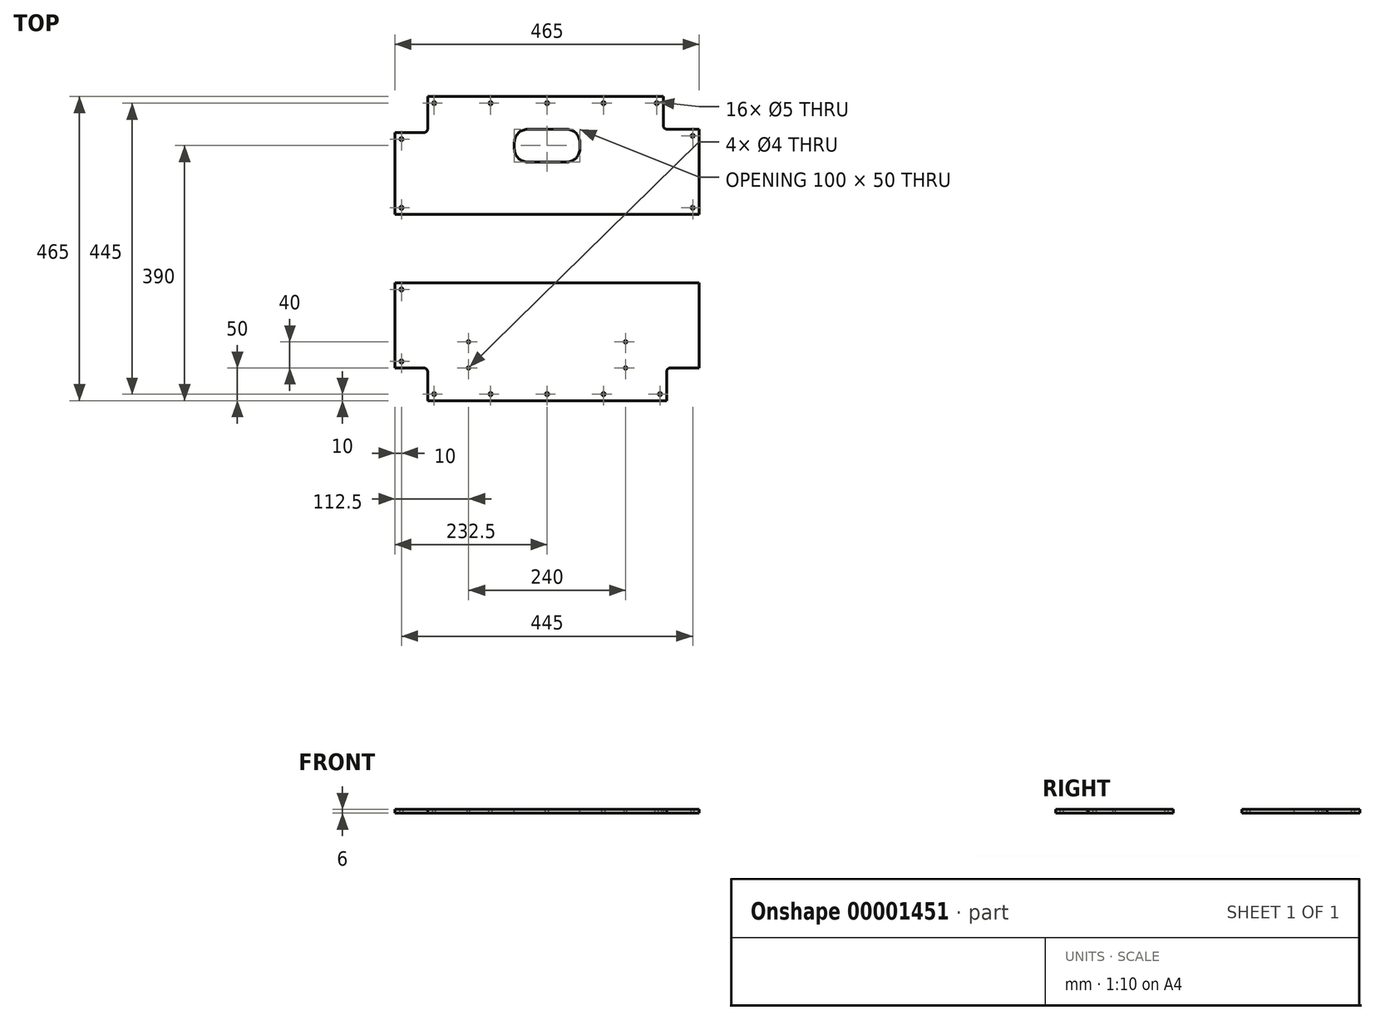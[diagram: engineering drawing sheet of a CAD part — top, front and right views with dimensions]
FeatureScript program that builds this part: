
annotation { "Feature Type Name" : "Feature", "Feature Type Description" : "" }
export const myFeature = defineFeature(function(context is Context, id is Id, definition is map)
    precondition{}
    {
        {
            var Q0;
            Q0=qCreatedBy(makeId("Top.planeOp"),FACE);
            var sketch = newSketch(context, id + "F0", { "sketchPlane" : qUnion([Q0])});
            skLineSegment(sketch, "E0.rect.bottom", {"start": v(212.5, 212.5) * mm, "end": v(-212.5, 212.5) * mm, "construction": true});
            skLineSegment(sketch, "E0.rect.top", {"start": v(212.5, -212.5) * mm, "end": v(-212.5, -212.5) * mm, "construction": true});
            skLineSegment(sketch, "E0.rect.left", {"start": v(212.5, 212.5) * mm, "end": v(212.5, -212.5) * mm, "construction": true});
            skLineSegment(sketch, "E0.rect.right", {"start": v(-212.5, 212.5) * mm, "end": v(-212.5, -212.5) * mm, "construction": true});
            skPoint(sketch, "E0.rect.middle", {"position": v(0, 0) * mm});
            skLineSegment(sketch, "E1.rect.bottom", {"start": v(232.5, 232.5) * mm, "end": v(-232.5, 232.5) * mm, "construction": true});
            skLineSegment(sketch, "E1.rect.top", {"start": v(232.5, -232.5) * mm, "end": v(-232.5, -232.5) * mm, "construction": true});
            skLineSegment(sketch, "E1.rect.left", {"start": v(232.5, 232.5) * mm, "end": v(232.5, -232.5) * mm, "construction": true});
            skLineSegment(sketch, "E1.rect.right", {"start": v(-232.5, 232.5) * mm, "end": v(-232.5, -232.5) * mm, "construction": true});
            skLineSegment(sketch, "E2", {"start": v(-212.5, 212.5) * mm, "end": v(-232.5, 212.5) * mm, "construction": true});
            skLineSegment(sketch, "E3", {"start": v(-212.5, 232.5) * mm, "end": v(-212.5, 212.5) * mm, "construction": true});
            skLineSegment(sketch, "E4", {"start": v(-212.5, -212.5) * mm, "end": v(-232.5, -212.5) * mm, "construction": true});
            skLineSegment(sketch, "E5", {"start": v(-212.5, -232.5) * mm, "end": v(-212.5, -212.5) * mm, "construction": true});
            skLineSegment(sketch, "E6", {"start": v(212.5, -212.5) * mm, "end": v(212.5, -232.5) * mm, "construction": true});
            skLineSegment(sketch, "E7", {"start": v(232.5, -212.5) * mm, "end": v(212.5, -212.5) * mm, "construction": true});
            skLineSegment(sketch, "E8", {"start": v(212.5, 212.5) * mm, "end": v(212.5, 232.5) * mm, "construction": true});
            skLineSegment(sketch, "E9", {"start": v(232.5, 212.5) * mm, "end": v(212.5, 212.5) * mm, "construction": true});
            skLineSegment(sketch, "E10", {"start": v(177.5, 232.5) * mm, "end": v(177.5, 182.5) * mm});
            skLineSegment(sketch, "E11", {"start": v(177.5, 182.5) * mm, "end": v(232.5, 182.5) * mm});
            skLineSegment(sketch, "E12", {"start": v(232.5, 182.5) * mm, "end": v(232.5, 52.5) * mm});
            skLineSegment(sketch, "E13", {"start": v(232.5, 52.5) * mm, "end": v(-232.5, 52.5) * mm});
            skLineSegment(sketch, "E14", {"start": v(-232.5, 52.5) * mm, "end": v(-232.5, 177.5) * mm});
            skLineSegment(sketch, "E15", {"start": v(-232.5, 177.5) * mm, "end": v(-182.5, 177.5) * mm});
            skLineSegment(sketch, "E16", {"start": v(-182.5, 177.5) * mm, "end": v(-182.5, 232.5) * mm});
            skLineSegment(sketch, "E17", {"start": v(-182.5, 232.5) * mm, "end": v(177.5, 232.5) * mm});
            skLineSegment(sketch, "E18", {"start": v(-232.5, -52.5) * mm, "end": v(232.5, -52.5) * mm});
            skLineSegment(sketch, "E19", {"start": v(232.5, -52.5) * mm, "end": v(232.5, -182.5) * mm});
            skLineSegment(sketch, "E20", {"start": v(232.5, -182.5) * mm, "end": v(182.5, -182.5) * mm});
            skLineSegment(sketch, "E21", {"start": v(182.5, -182.5) * mm, "end": v(182.5, -232.5) * mm});
            skLineSegment(sketch, "E22", {"start": v(182.5, -232.5) * mm, "end": v(-182.5, -232.5) * mm});
            skLineSegment(sketch, "E23", {"start": v(-182.5, -232.5) * mm, "end": v(-182.5, -182.5) * mm});
            skLineSegment(sketch, "E24", {"start": v(-182.5, -182.5) * mm, "end": v(-232.5, -182.5) * mm});
            skLineSegment(sketch, "E25", {"start": v(-232.5, -182.5) * mm, "end": v(-232.5, -52.5) * mm});
            skLineSegment(sketch, "E26", {"start": v(-182.5, -182.5) * mm, "end": v(182.5, -182.5) * mm, "construction": true});
            skSolve(sketch);
        }
        {
            var Q0;
            {Q0=qUnion([makeQuery(id+"F0.imprint","IMPRINT",FACE,{"disambiguationData":[TD([[makeQuery(id+"F0.imprint","IMPRINT",EDGE,{"derivedFrom":sQuery(id+"F0.wireOp",EDGE,"E10")}),-1.0]])]}),makeQuery(id+"F0.imprint","IMPRINT",FACE,{"disambiguationData":[TD([[makeQuery(id+"F0.imprint","IMPRINT",EDGE,{"derivedFrom":sQuery(id+"F0.wireOp",EDGE,"E18")}),-1.0]])]})]);}
            extrude(context, id + "F1", {"entities" : qUnion([Q0]), "depth" : 6 * mm});
        }
        {
            var Q0;
            Q0=makeQuery(id+"F1.opExtrude","SWEPT_EDGE",EDGE,{"disambiguationData":[OSD([sQuery(id+"F0.wireOp",EDGE,"E23"),sQuery(id+"F0.wireOp",EDGE,"E24")])]});
            var Q1;
            Q1=makeQuery(id+"F1.opExtrude","SWEPT_EDGE",EDGE,{"disambiguationData":[OSD([sQuery(id+"F0.wireOp",EDGE,"E20"),sQuery(id+"F0.wireOp",EDGE,"E21")])]});
            var Q2;
            Q2=makeQuery(id+"F1.opExtrude","SWEPT_EDGE",EDGE,{"disambiguationData":[OSD([sQuery(id+"F0.wireOp",EDGE,"E10"),sQuery(id+"F0.wireOp",EDGE,"E11")])]});
            var Q3;
            Q3=makeQuery(id+"F1.opExtrude","SWEPT_EDGE",EDGE,{"disambiguationData":[OSD([sQuery(id+"F0.wireOp",EDGE,"E15"),sQuery(id+"F0.wireOp",EDGE,"E16")])]});
            fillet(context, id + "F2", {"entities" : qUnion([Q0, Q1, Q2, Q3]), "radius" : 6 * mm, "tangentPropagation" : true, "allowEdgeOverflow" : false});
        }
        {
            var Q0;
            Q0=makeQuery(id+"F1.opExtrude","CAP_FACE",FACE,{"disambiguationData":[OSD([sQuery(id+"F0.wireOp",EDGE,"E18"),sQuery(id+"F0.wireOp",EDGE,"E19"),sQuery(id+"F0.wireOp",EDGE,"E20"),sQuery(id+"F0.wireOp",EDGE,"E21"),sQuery(id+"F0.wireOp",EDGE,"E22"),sQuery(id+"F0.wireOp",EDGE,"E23"),sQuery(id+"F0.wireOp",EDGE,"E24"),sQuery(id+"F0.wireOp",EDGE,"E25")])],"isStart":false});
            var sketch = newSketch(context, id + "F3", { "sketchPlane" : qUnion([Q0])});
            skLineSegment(sketch, "E27", {"start": v(-182.5, -222.5) * mm, "end": v(-172.5, -222.5) * mm, "construction": true});
            skLineSegment(sketch, "E28", {"start": v(-172.5, -222.5) * mm, "end": v(-86.25, -222.5) * mm, "construction": true});
            skLineSegment(sketch, "E29", {"start": v(-86.25, -222.5) * mm, "end": v(0, -222.5) * mm, "construction": true});
            skLineSegment(sketch, "E30", {"start": v(0, -222.5) * mm, "end": v(86.25, -222.5) * mm, "construction": true});
            skLineSegment(sketch, "E31", {"start": v(86.25, -222.5) * mm, "end": v(172.5, -222.5) * mm, "construction": true});
            skLineSegment(sketch, "E32", {"start": v(172.5, -222.5) * mm, "end": v(182.5, -222.5) * mm, "construction": true});
            skLineSegment(sketch, "E33", {"start": v(0, -222.5) * mm, "end": v(0, -232.5) * mm, "construction": true});
            skCircle(sketch, "E34", {"center": v(-172.5, -222.5) * mm, "radius": 2.5 * mm});
            skCircle(sketch, "E35", {"center": v(-86.25, -222.5) * mm, "radius": 2.5 * mm});
            skCircle(sketch, "E36", {"center": v(0, -222.5) * mm, "radius": 2.5 * mm});
            skCircle(sketch, "E37", {"center": v(86.25, -222.5) * mm, "radius": 2.5 * mm});
            skCircle(sketch, "E38", {"center": v(172.5, -222.5) * mm, "radius": 2.5 * mm});
            skLineSegment(sketch, "E39", {"start": v(-222.5, -52.5) * mm, "end": v(-222.5, -62.5) * mm, "construction": true});
            skLineSegment(sketch, "E40", {"start": v(-222.5, -62.5) * mm, "end": v(-222.5, -172.5) * mm, "construction": true});
            skLineSegment(sketch, "E41", {"start": v(-222.5, -172.5) * mm, "end": v(-222.5, -182.5) * mm, "construction": true});
            skLineSegment(sketch, "E42", {"start": v(-222.5, -62.5) * mm, "end": v(-232.5, -62.5) * mm, "construction": true});
            skLineSegment(sketch, "E43", {"start": v(-222.5, -172.5) * mm, "end": v(-232.5, -172.5) * mm, "construction": true});
            skLineSegment(sketch, "E44", {"start": v(0, -222.5) * mm, "end": v(0, -52.5) * mm, "construction": true});
            skCircle(sketch, "E45", {"center": v(-222.5, -62.5) * mm, "radius": 2.5 * mm});
            skCircle(sketch, "E46", {"center": v(-222.5, -172.5) * mm, "radius": 2.5 * mm});
            skCircle(sketch, "E47.0.MirrorC", {"center": v(222.5, -62.5) * mm, "radius": 2.5 * mm});
            skCircle(sketch, "E47.1.MirrorC", {"center": v(222.5, -172.5) * mm, "radius": 2.5 * mm});
            skSolve(sketch);
        }
        {
            var Q0;
            {Q0=qUnion([makeQuery(id+"F3.imprint","IMPRINT",FACE,{"disambiguationData":[TD([[makeQuery(id+"F3.imprint","IMPRINT",EDGE,{"derivedFrom":sQuery(id+"F3.wireOp",EDGE,"E34")}),1.0]])]}),makeQuery(id+"F3.imprint","IMPRINT",FACE,{"disambiguationData":[TD([[makeQuery(id+"F3.imprint","IMPRINT",EDGE,{"derivedFrom":sQuery(id+"F3.wireOp",EDGE,"E35")}),1.0]])]}),makeQuery(id+"F3.imprint","IMPRINT",FACE,{"disambiguationData":[TD([[makeQuery(id+"F3.imprint","IMPRINT",EDGE,{"derivedFrom":sQuery(id+"F3.wireOp",EDGE,"E36")}),1.0]])]}),makeQuery(id+"F3.imprint","IMPRINT",FACE,{"disambiguationData":[TD([[makeQuery(id+"F3.imprint","IMPRINT",EDGE,{"derivedFrom":sQuery(id+"F3.wireOp",EDGE,"E37")}),1.0]])]}),makeQuery(id+"F3.imprint","IMPRINT",FACE,{"disambiguationData":[TD([[makeQuery(id+"F3.imprint","IMPRINT",EDGE,{"derivedFrom":sQuery(id+"F3.wireOp",EDGE,"E38")}),1.0]])]}),makeQuery(id+"F3.imprint","IMPRINT",FACE,{"disambiguationData":[TD([[makeQuery(id+"F3.imprint","IMPRINT",EDGE,{"derivedFrom":sQuery(id+"F3.wireOp",EDGE,"E45")}),1.0]])]}),makeQuery(id+"F3.imprint","IMPRINT",FACE,{"disambiguationData":[TD([[makeQuery(id+"F3.imprint","IMPRINT",EDGE,{"derivedFrom":sQuery(id+"F3.wireOp",EDGE,"E46")}),1.0]])]}),makeQuery(id+"F3.imprint","IMPRINT",FACE,{"disambiguationData":[TD([[makeQuery(id+"F3.imprint","IMPRINT",EDGE,{"derivedFrom":sQuery(id+"F3.wireOp",EDGE,"E47.0.MirrorC")}),-1.0]])]}),makeQuery(id+"F3.imprint","IMPRINT",FACE,{"disambiguationData":[TD([[makeQuery(id+"F3.imprint","IMPRINT",EDGE,{"derivedFrom":sQuery(id+"F3.wireOp",EDGE,"E47.1.MirrorC")}),-1.0]])]})]);}
            extrude(context, id + "F4", {"entities" : qUnion([Q0]), "operationType" : NewBodyOperationType.REMOVE, "endBound" : BoundingType.THROUGH_ALL, "oppositeDirection" : true, "depth" : 25 * mm});
        }
        {
            var Q0;
            Q0=makeQuery(id+"F1.opExtrude","CAP_FACE",FACE,{"disambiguationData":[OSD([sQuery(id+"F0.wireOp",EDGE,"E18"),sQuery(id+"F0.wireOp",EDGE,"E19"),sQuery(id+"F0.wireOp",EDGE,"E20"),sQuery(id+"F0.wireOp",EDGE,"E21"),sQuery(id+"F0.wireOp",EDGE,"E22"),sQuery(id+"F0.wireOp",EDGE,"E23"),sQuery(id+"F0.wireOp",EDGE,"E24"),sQuery(id+"F0.wireOp",EDGE,"E25")])],"isStart":false});
            var sketch = newSketch(context, id + "F5", { "sketchPlane" : qUnion([Q0])});
            skLineSegment(sketch, "E48", {"start": v(0, -232.5) * mm, "end": v(0, -162.5) * mm, "construction": true});
            skLineSegment(sketch, "E49.rect.bottom", {"start": v(120, -142.5) * mm, "end": v(-120, -142.5) * mm, "construction": true});
            skLineSegment(sketch, "E49.rect.top", {"start": v(120, -182.5) * mm, "end": v(-120, -182.5) * mm, "construction": true});
            skLineSegment(sketch, "E49.rect.left", {"start": v(120, -142.5) * mm, "end": v(120, -182.5) * mm, "construction": true});
            skLineSegment(sketch, "E49.rect.right", {"start": v(-120, -142.5) * mm, "end": v(-120, -182.5) * mm, "construction": true});
            skPoint(sketch, "E49.rect.middle", {"position": v(0, -162.5) * mm});
            skCircle(sketch, "E50", {"center": v(-120, -142.5) * mm, "radius": 2 * mm});
            skCircle(sketch, "E51", {"center": v(120, -142.5) * mm, "radius": 2 * mm});
            skCircle(sketch, "E52", {"center": v(-120, -182.5) * mm, "radius": 2 * mm});
            skCircle(sketch, "E53", {"center": v(120, -182.5) * mm, "radius": 2 * mm});
            skSolve(sketch);
        }
        {
            var Q0;
            {Q0=qUnion([makeQuery(id+"F5.imprint","IMPRINT",FACE,{"disambiguationData":[TD([[makeQuery(id+"F5.imprint","IMPRINT",EDGE,{"derivedFrom":sQuery(id+"F5.wireOp",EDGE,"E50")}),1.0]])]}),makeQuery(id+"F5.imprint","IMPRINT",FACE,{"disambiguationData":[TD([[makeQuery(id+"F5.imprint","IMPRINT",EDGE,{"derivedFrom":sQuery(id+"F5.wireOp",EDGE,"E51")}),1.0]])]}),makeQuery(id+"F5.imprint","IMPRINT",FACE,{"disambiguationData":[TD([[makeQuery(id+"F5.imprint","IMPRINT",EDGE,{"derivedFrom":sQuery(id+"F5.wireOp",EDGE,"E52")}),1.0]])]}),makeQuery(id+"F5.imprint","IMPRINT",FACE,{"disambiguationData":[TD([[makeQuery(id+"F5.imprint","IMPRINT",EDGE,{"derivedFrom":sQuery(id+"F5.wireOp",EDGE,"E53")}),1.0]])]})]);}
            extrude(context, id + "F6", {"entities" : qUnion([Q0]), "operationType" : NewBodyOperationType.REMOVE, "endBound" : BoundingType.THROUGH_ALL, "oppositeDirection" : true, "depth" : 25 * mm});
        }
        {
            var Q0;
            Q0=makeQuery(id+"F1.opExtrude","CAP_FACE",FACE,{"disambiguationData":[OSD([sQuery(id+"F0.wireOp",EDGE,"E10"),sQuery(id+"F0.wireOp",EDGE,"E11"),sQuery(id+"F0.wireOp",EDGE,"E12"),sQuery(id+"F0.wireOp",EDGE,"E13"),sQuery(id+"F0.wireOp",EDGE,"E14"),sQuery(id+"F0.wireOp",EDGE,"E15"),sQuery(id+"F0.wireOp",EDGE,"E16"),sQuery(id+"F0.wireOp",EDGE,"E17")])],"isStart":false});
            var sketch = newSketch(context, id + "F7", { "sketchPlane" : qUnion([Q0])});
            skLineSegment(sketch, "E54", {"start": v(-182.5, 222.5) * mm, "end": v(-172.5, 222.5) * mm, "construction": true});
            skLineSegment(sketch, "E55", {"start": v(-172.5, 222.5) * mm, "end": v(-86.25, 222.5) * mm, "construction": true});
            skLineSegment(sketch, "E56", {"start": v(-86.25, 222.5) * mm, "end": v(0, 222.5) * mm, "construction": true});
            skLineSegment(sketch, "E57", {"start": v(0, 222.5) * mm, "end": v(0, 232.5) * mm, "construction": true});
            skLineSegment(sketch, "E58", {"start": v(0, 222.5) * mm, "end": v(0, 52.5) * mm, "construction": true});
            skLineSegment(sketch, "E59", {"start": v(0, 222.5) * mm, "end": v(86.25, 222.5) * mm, "construction": true});
            skLineSegment(sketch, "E60", {"start": v(86.25, 222.5) * mm, "end": v(167.5, 222.5) * mm, "construction": true});
            skLineSegment(sketch, "E61", {"start": v(167.5, 222.5) * mm, "end": v(177.5, 222.5) * mm, "construction": true});
            skLineSegment(sketch, "E62", {"start": v(-222.5, 177.5) * mm, "end": v(-222.5, 167.5) * mm, "construction": true});
            skLineSegment(sketch, "E63", {"start": v(-222.5, 167.5) * mm, "end": v(-222.5, 62.5) * mm, "construction": true});
            skLineSegment(sketch, "E64", {"start": v(-222.5, 62.5) * mm, "end": v(-222.5, 52.5) * mm, "construction": true});
            skLineSegment(sketch, "E65", {"start": v(-222.5, 167.5) * mm, "end": v(-232.5, 167.5) * mm, "construction": true});
            skLineSegment(sketch, "E66", {"start": v(222.5, 182.5) * mm, "end": v(222.5, 172.5) * mm, "construction": true});
            skLineSegment(sketch, "E67", {"start": v(222.5, 172.5) * mm, "end": v(232.5, 172.5) * mm, "construction": true});
            skLineSegment(sketch, "E68", {"start": v(222.5, 172.5) * mm, "end": v(222.5, 62.5) * mm, "construction": true});
            skLineSegment(sketch, "E69", {"start": v(222.5, 62.5) * mm, "end": v(232.5, 62.5) * mm, "construction": true});
            skCircle(sketch, "E70", {"center": v(-222.5, 167.5) * mm, "radius": 2.5 * mm});
            skCircle(sketch, "E71", {"center": v(-222.5, 62.5) * mm, "radius": 2.5 * mm});
            skCircle(sketch, "E72", {"center": v(-172.5, 222.5) * mm, "radius": 2.5 * mm});
            skCircle(sketch, "E73", {"center": v(-86.25, 222.5) * mm, "radius": 2.5 * mm});
            skCircle(sketch, "E74", {"center": v(0, 222.5) * mm, "radius": 2.5 * mm});
            skCircle(sketch, "E75", {"center": v(86.25, 222.5) * mm, "radius": 2.5 * mm});
            skCircle(sketch, "E76", {"center": v(167.5, 222.5) * mm, "radius": 2.5 * mm});
            skCircle(sketch, "E77", {"center": v(222.5, 172.5) * mm, "radius": 2.5 * mm});
            skCircle(sketch, "E78", {"center": v(222.5, 62.5) * mm, "radius": 2.5 * mm});
            skLineSegment(sketch, "E79", {"start": v(222.5, 62.5) * mm, "end": v(222.5, 52.5) * mm, "construction": true});
            skLineSegment(sketch, "E80", {"start": v(-222.5, 62.5) * mm, "end": v(-232.5, 62.5) * mm, "construction": true});
            skSolve(sketch);
        }
        {
            var Q0;
            {Q0=qUnion([makeQuery(id+"F7.imprint","IMPRINT",FACE,{"disambiguationData":[TD([[makeQuery(id+"F7.imprint","IMPRINT",EDGE,{"derivedFrom":sQuery(id+"F7.wireOp",EDGE,"E70")}),1.0]])]}),makeQuery(id+"F7.imprint","IMPRINT",FACE,{"disambiguationData":[TD([[makeQuery(id+"F7.imprint","IMPRINT",EDGE,{"derivedFrom":sQuery(id+"F7.wireOp",EDGE,"E71")}),1.0]])]}),makeQuery(id+"F7.imprint","IMPRINT",FACE,{"disambiguationData":[TD([[makeQuery(id+"F7.imprint","IMPRINT",EDGE,{"derivedFrom":sQuery(id+"F7.wireOp",EDGE,"E72")}),1.0]])]}),makeQuery(id+"F7.imprint","IMPRINT",FACE,{"disambiguationData":[TD([[makeQuery(id+"F7.imprint","IMPRINT",EDGE,{"derivedFrom":sQuery(id+"F7.wireOp",EDGE,"E73")}),1.0]])]}),makeQuery(id+"F7.imprint","IMPRINT",FACE,{"disambiguationData":[TD([[makeQuery(id+"F7.imprint","IMPRINT",EDGE,{"derivedFrom":sQuery(id+"F7.wireOp",EDGE,"E74")}),1.0]])]}),makeQuery(id+"F7.imprint","IMPRINT",FACE,{"disambiguationData":[TD([[makeQuery(id+"F7.imprint","IMPRINT",EDGE,{"derivedFrom":sQuery(id+"F7.wireOp",EDGE,"E75")}),1.0]])]}),makeQuery(id+"F7.imprint","IMPRINT",FACE,{"disambiguationData":[TD([[makeQuery(id+"F7.imprint","IMPRINT",EDGE,{"derivedFrom":sQuery(id+"F7.wireOp",EDGE,"E76")}),1.0]])]}),makeQuery(id+"F7.imprint","IMPRINT",FACE,{"disambiguationData":[TD([[makeQuery(id+"F7.imprint","IMPRINT",EDGE,{"derivedFrom":sQuery(id+"F7.wireOp",EDGE,"E77")}),1.0]])]}),makeQuery(id+"F7.imprint","IMPRINT",FACE,{"disambiguationData":[TD([[makeQuery(id+"F7.imprint","IMPRINT",EDGE,{"derivedFrom":sQuery(id+"F7.wireOp",EDGE,"E78")}),1.0]])]})]);}
            extrude(context, id + "F8", {"entities" : qUnion([Q0]), "operationType" : NewBodyOperationType.REMOVE, "endBound" : BoundingType.THROUGH_ALL, "oppositeDirection" : true, "depth" : 25 * mm});
        }
        {
            var Q0;
            Q0=makeQuery(id+"F1.opExtrude","CAP_FACE",FACE,{"disambiguationData":[OSD([sQuery(id+"F0.wireOp",EDGE,"E10"),sQuery(id+"F0.wireOp",EDGE,"E11"),sQuery(id+"F0.wireOp",EDGE,"E12"),sQuery(id+"F0.wireOp",EDGE,"E13"),sQuery(id+"F0.wireOp",EDGE,"E14"),sQuery(id+"F0.wireOp",EDGE,"E15"),sQuery(id+"F0.wireOp",EDGE,"E16"),sQuery(id+"F0.wireOp",EDGE,"E17")])],"isStart":false});
            var sketch = newSketch(context, id + "F9", { "sketchPlane" : qUnion([Q0])});
            skLineSegment(sketch, "E81", {"start": v(0, 232.5) * mm, "end": v(0, 157.5) * mm, "construction": true});
            skLineSegment(sketch, "E82.rect.bottom", {"start": v(50, 182.5) * mm, "end": v(-50, 182.5) * mm});
            skLineSegment(sketch, "E82.rect.top", {"start": v(50, 132.5) * mm, "end": v(-50, 132.5) * mm});
            skLineSegment(sketch, "E82.rect.left", {"start": v(50, 182.5) * mm, "end": v(50, 132.5) * mm});
            skLineSegment(sketch, "E82.rect.right", {"start": v(-50, 182.5) * mm, "end": v(-50, 132.5) * mm});
            skPoint(sketch, "E82.rect.middle", {"position": v(0, 157.5) * mm});
            skSolve(sketch);
        }
        {
            var Q0;
            Q0=makeQuery(id+"F9.imprint","IMPRINT",FACE,{"disambiguationData":[TD([[makeQuery(id+"F9.imprint","IMPRINT",EDGE,{"derivedFrom":sQuery(id+"F9.wireOp",EDGE,"E82.rect.bottom")}),1.0]])]});
            extrude(context, id + "F10", {"entities" : qUnion([Q0]), "operationType" : NewBodyOperationType.REMOVE, "endBound" : BoundingType.THROUGH_ALL, "oppositeDirection" : true, "depth" : 25 * mm});
        }
        {
            var Q0;
            Q0=makeQuery(id+"F10.boolean.opBoolean","COPY",EDGE,{"derivedFrom":makeQuery(id+"F10.opExtrude","SWEPT_EDGE",EDGE,{"disambiguationData":[OSD([sQuery(id+"F9.wireOp",EDGE,"E82.rect.bottom"),sQuery(id+"F9.wireOp",EDGE,"E82.rect.right")])]})});
            var Q1;
            Q1=makeQuery(id+"F10.boolean.opBoolean","COPY",EDGE,{"derivedFrom":makeQuery(id+"F10.opExtrude","SWEPT_EDGE",EDGE,{"disambiguationData":[OSD([sQuery(id+"F9.wireOp",EDGE,"E82.rect.bottom"),sQuery(id+"F9.wireOp",EDGE,"E82.rect.left")])]})});
            var Q2;
            Q2=makeQuery(id+"F10.boolean.opBoolean","COPY",EDGE,{"derivedFrom":makeQuery(id+"F10.opExtrude","SWEPT_EDGE",EDGE,{"disambiguationData":[OSD([sQuery(id+"F9.wireOp",EDGE,"E82.rect.top"),sQuery(id+"F9.wireOp",EDGE,"E82.rect.left")])]})});
            var Q3;
            Q3=makeQuery(id+"F10.boolean.opBoolean","COPY",EDGE,{"derivedFrom":makeQuery(id+"F10.opExtrude","SWEPT_EDGE",EDGE,{"disambiguationData":[OSD([sQuery(id+"F9.wireOp",EDGE,"E82.rect.top"),sQuery(id+"F9.wireOp",EDGE,"E82.rect.right")])]})});
            fillet(context, id + "F11", {"entities" : qUnion([Q0, Q1, Q2, Q3]), "radius" : 20 * mm, "tangentPropagation" : true, "allowEdgeOverflow" : false});
        }
    });
